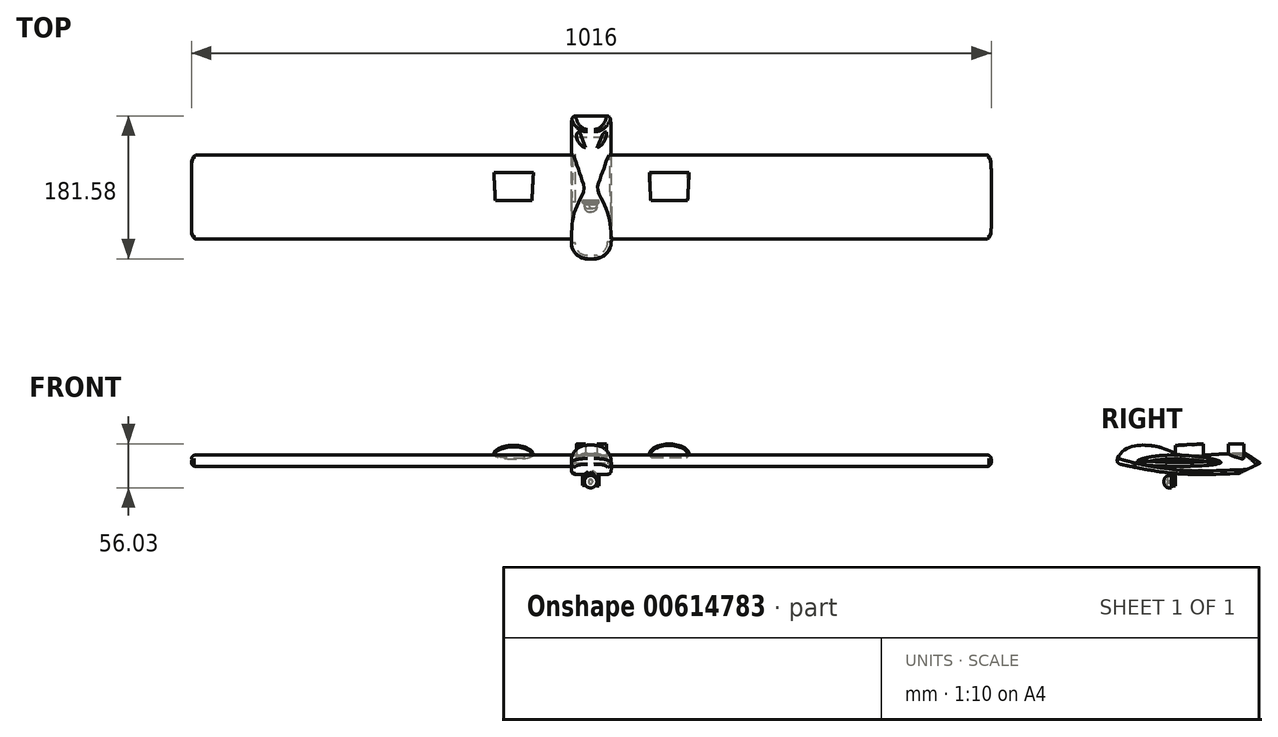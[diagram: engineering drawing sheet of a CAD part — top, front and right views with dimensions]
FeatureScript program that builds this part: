
annotation { "Feature Type Name" : "Feature", "Feature Type Description" : "" }
export const myFeature = defineFeature(function(context is Context, id is Id, definition is map)
    precondition{}
    {
        {
            var Q0;
            Q0=qCreatedBy(makeId("Right.planeOp"),FACE);
            var sketch = newSketch(context, id + "F0", { "sketchPlane" : qUnion([Q0])});
            skFitSpline(sketch, "E0", {"points": [v(-76.17, 0) * mm, v(-67.9, 13.97) * mm, v(-51.93, 21.87) * mm, v(-19.6, 20.12) * mm, v(8.24, 10.94) * mm, v(51.37, 11.1) * mm, v(89.2, 12.57) * mm], "startDerivative": vector(55.43, 121.29) * mm, "endDerivative": vector(189.56, 4.65) * mm});
            skLineSegment(sketch, "E1", {"start": v(89.2, 12.57) * mm, "end": v(107.68, 0) * mm});
            skLineSegment(sketch, "E2", {"start": v(107.68, 0) * mm, "end": v(80.59, -13.1) * mm});
            skFitSpline(sketch, "E3", {"points": [v(80.59, -13.1) * mm, v(0, -13.1) * mm, v(-76.17, 0) * mm], "startDerivative": vector(-160.91, -6.7) * mm, "endDerivative": vector(-152.56, 33.04) * mm});
            skSolve(sketch);
        }
        {
            var Q0;
            Q0=makeQuery(id+"F0.imprint","IMPRINT",FACE,{"disambiguationData":[TD([[makeQuery(id+"F0.imprint","IMPRINT",EDGE,{"derivedFrom":sQuery(id+"F0.wireOp",EDGE,"E0")}),-1.0]])]});
            extrude(context, id + "F1", {"entities" : qUnion([Q0]), "oppositeDirection" : true, "depth" : 25.4 * mm, "offsetDistance" : 25.4 * mm, "hasSecondDirection" : true, "secondDirectionOppositeDirection" : false, "secondDirectionDepth" : 25.4 * mm});
        }
        {
            var Q0;
            Q0=qCreatedBy(makeId("Right.planeOp"),FACE);
            var sketch = newSketch(context, id + "F2", { "sketchPlane" : qUnion([Q0])});
            skFitSpline(sketch, "E4", {"points": [v(-46.93, 0) * mm, v(-11.06, 10.06) * mm, v(56.95, 0) * mm, v(-46.93, 0) * mm]});
            skSolve(sketch);
        }
        {
            var Q0;
            Q0 = qSketchRegion(id + "F2", true);
            extrude(context, id + "F3", {"entities" : qUnion([Q0]), "operationType" : NewBodyOperationType.ADD, "oppositeDirection" : true, "depth" : 508 * mm, "offsetDistance" : 25.4 * mm, "hasSecondDirection" : true, "secondDirectionOppositeDirection" : false, "secondDirectionDepth" : 508 * mm});
        }
        {
            var Q0;
            Q0=makeQuery(id+"F1.opExtrude","CAP_EDGE",EDGE,{"disambiguationData":[OSD([sQuery(id+"F0.wireOp",EDGE,"E0")])],"isStart":true});
            fillet(context, id + "F4", {"entities" : qUnion([Q0]), "radius" : 21.7 * mm, "tangentPropagation" : true, "allowEdgeOverflow" : false});
        }
        {
            var Q0;
            Q0=makeQuery(id+"F1.opExtrude","CAP_EDGE",EDGE,{"disambiguationData":[OSD([sQuery(id+"F0.wireOp",EDGE,"E0")])],"isStart":false});
            fillet(context, id + "F5", {"entities" : qUnion([Q0]), "radius" : 20.46 * mm, "tangentPropagation" : true, "allowEdgeOverflow" : false});
        }
        {
            var Q0;
            Q0=qCreatedBy(makeId("Front.planeOp"),FACE);
            var sketch = newSketch(context, id + "F6", { "sketchPlane" : qUnion([Q0])});
            skCircle(sketch, "E5", {"center": v(-0.8, -23.61) * mm, "radius": 7.92 * mm});
            skSolve(sketch);
        }
        {
            var Q0;
            Q0=makeQuery(id+"F6.imprint","IMPRINT",FACE,{"disambiguationData":[TD([[makeQuery(id+"F6.imprint","IMPRINT",EDGE,{"derivedFrom":sQuery(id+"F6.wireOp",EDGE,"E5")}),1.0]])]});
            extrude(context, id + "F7", {"entities" : qUnion([Q0]), "depth" : 14.32 * mm, "offsetDistance" : 25.4 * mm});
        }
        {
            var Q0;
            Q0=makeQuery(id+"F7.opExtrude","CAP_EDGE",EDGE,{"disambiguationData":[OSD([sQuery(id+"F6.wireOp",EDGE,"E5")])],"isStart":false});
            fillet(context, id + "F8", {"entities" : qUnion([Q0]), "radius" : 6.58 * mm, "tangentPropagation" : true, "allowEdgeOverflow" : false});
        }
        {
            var Q0;
            Q0=makeQuery(id+"F7.opExtrude","CAP_EDGE",EDGE,{"disambiguationData":[OSD([sQuery(id+"F6.wireOp",EDGE,"E5")])],"isStart":true});
            fillet(context, id + "F9", {"entities" : qUnion([Q0]), "radius" : 5.08 * mm, "tangentPropagation" : true, "allowEdgeOverflow" : false});
        }
        {
            var Q0;
            Q0=qCreatedBy(makeId("Front.planeOp"),FACE);
            var sketch = newSketch(context, id + "F10", { "sketchPlane" : qUnion([Q0])});
            skLineSegment(sketch, "E6", {"start": v(0, -11.18) * mm, "end": v(-8.14, -18.08) * mm});
            skLineSegment(sketch, "E7", {"start": v(-8.14, -18.08) * mm, "end": v(-8.14, -28.1) * mm});
            skLineSegment(sketch, "E8", {"start": v(-8.14, -28.1) * mm, "end": v(-10.82, -28.1) * mm});
            skLineSegment(sketch, "E9", {"start": v(-10.82, -28.1) * mm, "end": v(-10.82, -16.4) * mm});
            skLineSegment(sketch, "E10", {"start": v(-10.82, -16.4) * mm, "end": v(-4.07, -10.67) * mm});
            skPoint(sketch, "E10.endSnap0", {"position": v(-4.07, -14.63) * mm});
            skLineSegment(sketch, "E11", {"start": v(-4.07, -10.67) * mm, "end": v(0, -11.18) * mm});
            skSolve(sketch);
        }
        {
            var Q0;
            Q0=qCreatedBy(makeId("Front.planeOp"),FACE);
            var sketch = newSketch(context, id + "F11", { "sketchPlane" : qUnion([Q0])});
            skLineSegment(sketch, "E12", {"start": v(0, -11.1) * mm, "end": v(6.5, -18.21) * mm});
            skLineSegment(sketch, "E13", {"start": v(6.5, -18.21) * mm, "end": v(6.5, -28.83) * mm});
            skLineSegment(sketch, "E14", {"start": v(6.5, -28.83) * mm, "end": v(9.55, -28.83) * mm});
            skLineSegment(sketch, "E15", {"start": v(9.55, -28.83) * mm, "end": v(9.55, -16.51) * mm});
            skLineSegment(sketch, "E16", {"start": v(9.55, -16.51) * mm, "end": v(2.17, -10.19) * mm});
            skLineSegment(sketch, "E17", {"start": v(2.17, -10.19) * mm, "end": v(0, -11.1) * mm});
            skSolve(sketch);
        }
        {
            var Q0;
            Q0=makeQuery(id+"F11.imprint","IMPRINT",FACE,{"disambiguationData":[TD([[makeQuery(id+"F11.imprint","IMPRINT",EDGE,{"derivedFrom":sQuery(id+"F11.wireOp",EDGE,"E12")}),1.0]])]});
            extrude(context, id + "F12", {"entities" : qUnion([Q0]), "depth" : 2.83 * mm, "offsetDistance" : 25.4 * mm});
        }
        {
            var Q0;
            Q0=makeQuery(id+"F10.imprint","IMPRINT",FACE,{"disambiguationData":[TD([[makeQuery(id+"F10.imprint","IMPRINT",EDGE,{"derivedFrom":sQuery(id+"F10.wireOp",EDGE,"E6")}),-1.0]])]});
            extrude(context, id + "F13", {"entities" : qUnion([Q0]), "depth" : 2.82 * mm, "offsetDistance" : 25.4 * mm});
        }
        {
            var Q0;
            Q0=qCreatedBy(makeId("Top.planeOp"),FACE);
            var sketch = newSketch(context, id + "F14", { "sketchPlane" : qUnion([Q0])});
            skLineSegment(sketch, "E18", {"start": v(-20.68, 86.97) * mm, "end": v(-14.56, 67.28) * mm});
            skLineSegment(sketch, "E19", {"start": v(-14.56, 67.28) * mm, "end": v(-7.41, 67.28) * mm});
            skLineSegment(sketch, "E20", {"start": v(-7.41, 67.28) * mm, "end": v(-14.95, 87.36) * mm});
            skLineSegment(sketch, "E21", {"start": v(-14.95, 87.36) * mm, "end": v(-20.68, 86.97) * mm});
            skSolve(sketch);
        }
        {
            var Q0;
            Q0=qCreatedBy(makeId("Top.planeOp"),FACE);
            var sketch = newSketch(context, id + "F15", { "sketchPlane" : qUnion([Q0])});
            skLineSegment(sketch, "E22", {"start": v(20.64, 87.3) * mm, "end": v(13.76, 67.15) * mm});
            skLineSegment(sketch, "E23", {"start": v(13.76, 67.15) * mm, "end": v(7.2, 67.15) * mm});
            skLineSegment(sketch, "E24", {"start": v(7.2, 67.15) * mm, "end": v(15.87, 87.17) * mm});
            skLineSegment(sketch, "E25", {"start": v(15.87, 87.17) * mm, "end": v(20.64, 87.3) * mm});
            skSolve(sketch);
        }
        {
            var Q0;
            Q0 = qSketchRegion(id + "F14", true);
            extrude(context, id + "F16", {"entities" : qUnion([Q0]), "operationType" : NewBodyOperationType.ADD, "depth" : 24.28 * mm, "offsetDistance" : 25.4 * mm});
        }
        {
            var Q0;
            Q0=makeQuery(id+"F16.opExtrude","SWEPT_EDGE",EDGE,{"disambiguationData":[OSD([sQuery(id+"F14.wireOp",EDGE,"E18"),sQuery(id+"F14.wireOp",EDGE,"E19")])]});
            fillet(context, id + "F17", {"entities" : qUnion([Q0]), "radius" : 16.47 * mm, "tangentPropagation" : true, "allowEdgeOverflow" : false});
        }
        {
            var Q0;
            Q0 = qSketchRegion(id + "F15", true);
            extrude(context, id + "F18", {"entities" : qUnion([Q0]), "operationType" : NewBodyOperationType.ADD, "depth" : 24.3 * mm, "offsetDistance" : 25.4 * mm});
        }
        {
            var Q0;
            Q0=makeQuery(id+"F18.opExtrude","SWEPT_EDGE",EDGE,{"disambiguationData":[OSD([sQuery(id+"F15.wireOp",EDGE,"E22"),sQuery(id+"F15.wireOp",EDGE,"E23")])]});
            fillet(context, id + "F19", {"entities" : qUnion([Q0]), "radius" : 17.1 * mm, "tangentPropagation" : true, "allowEdgeOverflow" : false});
        }
        {
            var Q0;
            Q0=makeQuery(id+"F16.opExtrude","SWEPT_EDGE",EDGE,{"disambiguationData":[OSD([sQuery(id+"F14.wireOp",EDGE,"E18"),sQuery(id+"F14.wireOp",EDGE,"E21")])]});
            fillet(context, id + "F20", {"entities" : qUnion([Q0]), "radius" : 5.08 * mm, "tangentPropagation" : true, "allowEdgeOverflow" : false});
        }
        {
            var Q0;
            Q0=makeQuery(id+"F20.opFillet","BLEND_EDGE",EDGE,{"blendedFrom":[makeQuery(id+"F16.opExtrude","SWEPT_EDGE",EDGE,{"disambiguationData":[OSD([sQuery(id+"F14.wireOp",EDGE,"E18"),sQuery(id+"F14.wireOp",EDGE,"E21")])]}),makeQuery(id+"F16.opExtrude","SWEPT_FACE",FACE,{"disambiguationData":[OSD([sQuery(id+"F14.wireOp",EDGE,"E20")])]})],"blendedInto":[makeQuery(id+"F16.opExtrude","SWEPT_FACE",FACE,{"disambiguationData":[OSD([sQuery(id+"F14.wireOp",EDGE,"E20")])]})]});
            fillet(context, id + "F21", {"entities" : qUnion([Q0]), "radius" : 1.37 * mm, "tangentPropagation" : true, "allowEdgeOverflow" : false});
        }
        {
            var Q0;
            Q0=makeQuery(id+"F18.opExtrude","SWEPT_EDGE",EDGE,{"disambiguationData":[OSD([sQuery(id+"F15.wireOp",EDGE,"E24"),sQuery(id+"F15.wireOp",EDGE,"E25")])]});
            fillet(context, id + "F22", {"entities" : qUnion([Q0]), "radius" : 5.08 * mm, "tangentPropagation" : true, "allowEdgeOverflow" : false});
        }
        {
            var Q0;
            Q0=makeQuery(id+"F18.opExtrude","SWEPT_EDGE",EDGE,{"disambiguationData":[OSD([sQuery(id+"F15.wireOp",EDGE,"E22"),sQuery(id+"F15.wireOp",EDGE,"E25")])]});
            var Q1;
            Q1=makeQuery(id+"F1.opExtrude","SWEPT_FACE",FACE,{"disambiguationData":[OSD([sQuery(id+"F0.wireOp",EDGE,"E0")])]});
            fillet(context, id + "F23", {"entities" : qUnion([Q0, Q1]), "radius" : 5.08 * mm, "tangentPropagation" : true, "allowEdgeOverflow" : false});
        }
        {
            var Q0;
            Q0=qCreatedBy(makeId("Front.planeOp"),FACE);
            var sketch = newSketch(context, id + "F24", { "sketchPlane" : qUnion([Q0])});
            skFitSpline(sketch, "E26", {"points": [v(121.73, 10.19) * mm, v(98.98, 22.62) * mm, v(76.25, 10.12) * mm, v(121.73, 10.19) * mm]});
            skSolve(sketch);
        }
        {
            var Q0;
            Q0=qCreatedBy(makeId("Front.planeOp"),FACE);
            var sketch = newSketch(context, id + "F25", { "sketchPlane" : qUnion([Q0])});
            skFitSpline(sketch, "E27", {"points": [v(-76.02, 10.07) * mm, v(-98.37, 20.87) * mm, v(-121.26, 10.6) * mm, v(-76.02, 10.07) * mm]});
            skSolve(sketch);
        }
        {
            var Q0;
            Q0 = qSketchRegion(id + "F25", true);
            var Q1;
            Q1=sQuery(id+"F25.wireOp",EDGE,"E27");
            extrude(context, id + "F26", {"entities" : qUnion([Q0]), "surfaceEntities" : qUnion([Q1]), "oppositeDirection" : true, "depth" : 35.78 * mm, "offsetDistance" : 25.4 * mm, "hasDraft" : true, "draftAngle" : 3 * degree});
        }
        {
            var Q0;
            Q0 = qSketchRegion(id + "F24", true);
            extrude(context, id + "F27", {"entities" : qUnion([Q0]), "operationType" : NewBodyOperationType.ADD, "oppositeDirection" : true, "depth" : 35.8 * mm, "offsetDistance" : 25.4 * mm, "hasDraft" : true, "draftAngle" : 3 * degree});
        }
        {
            var Q0;
            Q0=makeQuery(id+"F3.opExtrude","CAP_EDGE",EDGE,{"disambiguationData":[OSD([sQuery(id+"F2.wireOp",EDGE,"E4")])],"isStart":true});
            fillet(context, id + "F28", {"entities" : qUnion([Q0]), "radius" : 4.97 * mm, "tangentPropagation" : true, "allowEdgeOverflow" : false});
        }
        {
            var Q0;
            Q0=makeQuery(id+"F3.opExtrude","CAP_EDGE",EDGE,{"disambiguationData":[OSD([sQuery(id+"F2.wireOp",EDGE,"E4")])],"isStart":false});
            fillet(context, id + "F29", {"entities" : qUnion([Q0]), "radius" : 5.08 * mm, "tangentPropagation" : true, "allowEdgeOverflow" : false});
        }
    });
